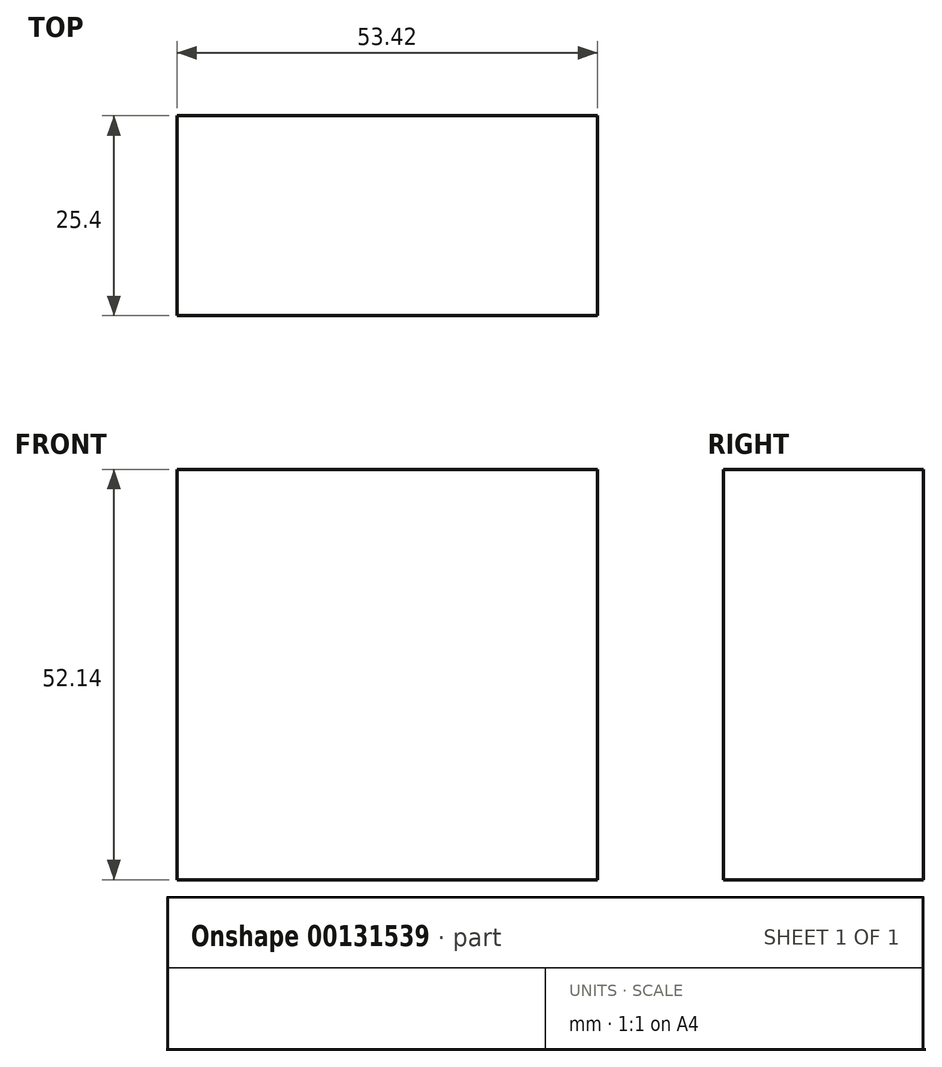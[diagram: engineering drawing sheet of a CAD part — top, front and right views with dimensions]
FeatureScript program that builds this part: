
annotation { "Feature Type Name" : "Feature", "Feature Type Description" : "" }
export const myFeature = defineFeature(function(context is Context, id is Id, definition is map)
    precondition{}
    {
        {
            var Q0;
            Q0=qCreatedBy(makeId("Front.planeOp"),FACE);
            var sketch = newSketch(context, id + "F0", { "sketchPlane" : qUnion([Q0])});
            skLineSegment(sketch, "E0.bottom", {"start": v(-26.7, 26.07) * mm, "end": v(26.7, 26.07) * mm});
            skLineSegment(sketch, "E0.top", {"start": v(-26.7, -26.07) * mm, "end": v(26.7, -26.07) * mm});
            skLineSegment(sketch, "E0.left", {"start": v(-26.7, 26.07) * mm, "end": v(-26.7, -26.07) * mm});
            skLineSegment(sketch, "E0.right", {"start": v(26.7, 26.07) * mm, "end": v(26.7, -26.07) * mm});
            skPoint(sketch, "E0.middle", {"position": v(0, 0) * mm});
            skSolve(sketch);
        }
        {
            var Q0;
            Q0=makeQuery(id+"F0.imprint","IMPRINT",FACE,{"disambiguationData":[TD([[makeQuery(id+"F0.imprint","IMPRINT",EDGE,{"derivedFrom":sQuery(id+"F0.wireOp",EDGE,"E0.bottom")}),-1.0]])]});
            extrude(context, id + "F1", {"entities" : qUnion([Q0]), "endBound" : BoundingType.SYMMETRIC, "depth" : 25.4 * mm});
        }
    });
